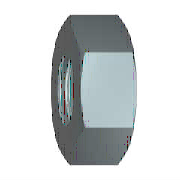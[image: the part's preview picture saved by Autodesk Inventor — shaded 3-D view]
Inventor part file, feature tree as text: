
AUTODESK INVENTOR PART (.ipt)
format: ipt  version: 2020 (Build 240168000, 168)  size: 166,912 bytes
history: native  units: mm (DEFAULTED — no unit token found)
features: sketch x3, other x2, extrude x1, hole x1, plane x1
ambient origin geometry x7: Origin, YZ Plane, XZ Plane, X Axis, Y Axis, Z Axis, Center Point
bodies: Solid1 (feature_tree)
feature tree (8):
  extrude  "Bryła"  Depth=11.547005mm
  other  "Faza1"
  hole  "Gwint"  [1 undecoded]
  other  "Work Axis1"
  plane  "Work Plane1"
  sketch  "Szkic1"
  sketch  "Szkic2"
  sketch  "Szkic3"
note: 1 required parameter value undecoded (feature->parameter linkage not recoverable at this tier; creation-order binding heuristic only, values carry confidence <= 0.55)
